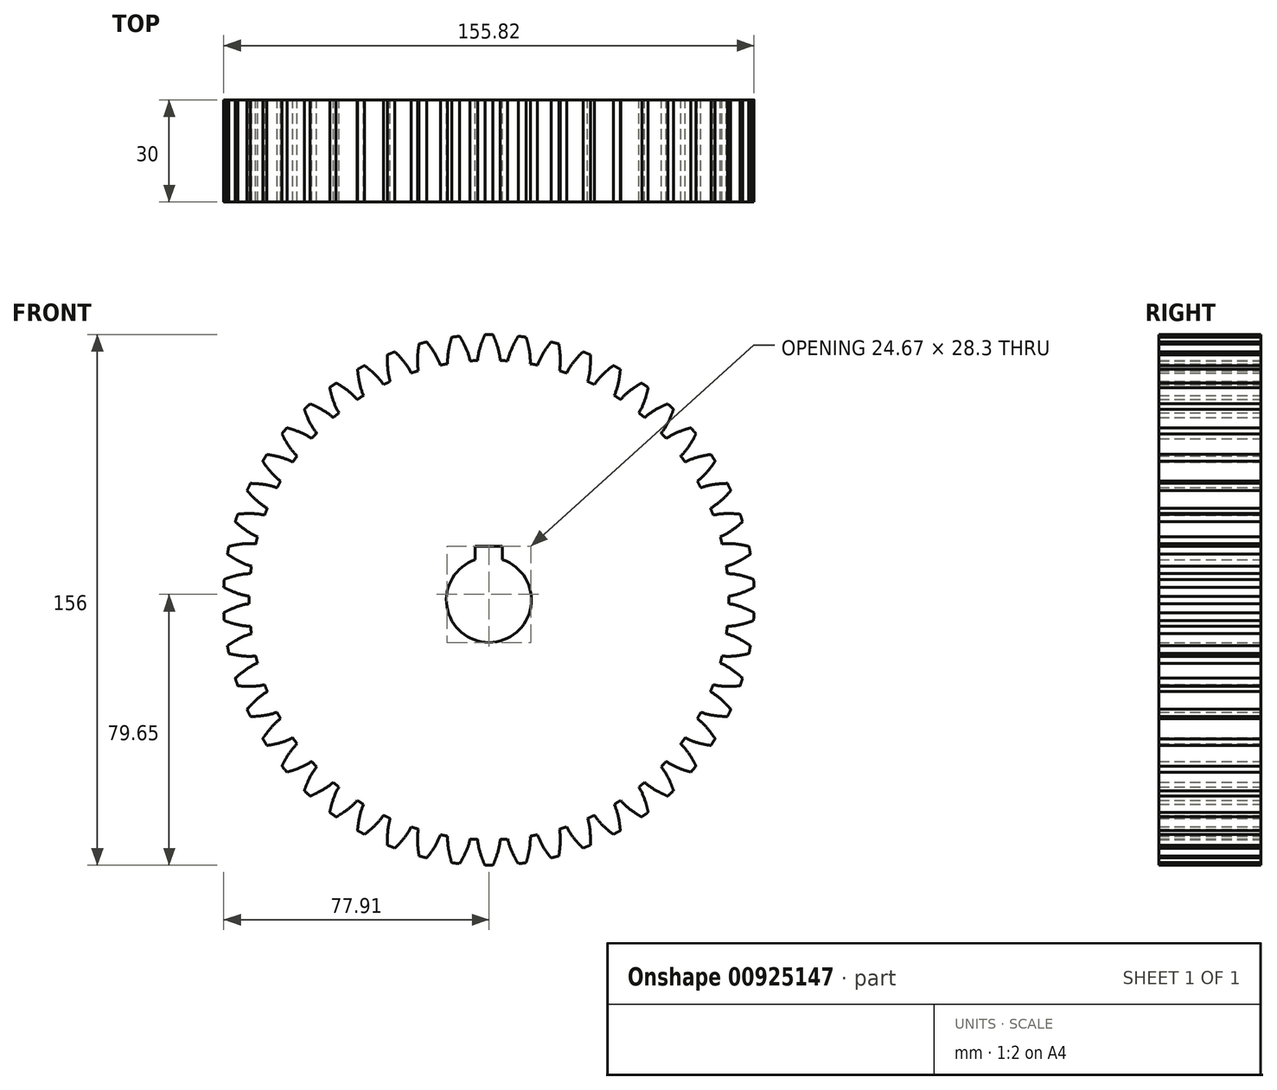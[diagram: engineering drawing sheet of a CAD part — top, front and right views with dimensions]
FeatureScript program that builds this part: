
annotation { "Feature Type Name" : "Feature", "Feature Type Description" : "" }
export const myFeature = defineFeature(function(context is Context, id is Id, definition is map)
    precondition{}
    {
        {
            var Q0;
            Q0=qCreatedBy(makeId("Front.planeOp"),FACE);
            var sketch = newSketch(context, id + "F0", { "sketchPlane" : qUnion([Q0])});
            skCircle(sketch, "E0", {"center": v(0, 0) * mm, "radius": 70.48 * mm});
            skSolve(sketch);
        }
        {
            var Q0;
            Q0 = qSketchRegion(id + "F0", true);
            extrude(context, id + "F1", {"entities" : qUnion([Q0]), "depth" : 30 * mm, "offsetDistance" : 25 * mm});
        }
        {
            var Q0;
            Q0=qCreatedBy(makeId("Front.planeOp"),FACE);
            var sketch = newSketch(context, id + "F2", { "sketchPlane" : qUnion([Q0])});
            skCircle(sketch, "E1", {"center": v(0, 0) * mm, "radius": 75 * mm, "construction": true});
            skArc(sketch, "E2", {"start": v(33.3, 62.11) * mm, "mid": v(22.01, 66.95) * mm, "end": v(10.05, 69.76) * mm, "construction": true});
            skLineSegment(sketch, "E3", {"start": v(-2.36, 74.96) * mm, "end": v(2.36, 74.96) * mm, "construction": true});
            skLineSegment(sketch, "E4", {"start": v(0, 0) * mm, "end": v(-2.36, 74.96) * mm, "construction": true});
            skLineSegment(sketch, "E5", {"start": v(-2.36, 74.96) * mm, "end": v(22.01, 66.95) * mm, "construction": true});
            skLineSegment(sketch, "E6", {"start": v(0, 0) * mm, "end": v(22.01, 66.95) * mm, "construction": true});
            skLineSegment(sketch, "E7.1.0", {"start": v(0, 0) * mm, "end": v(24.34, 66.14) * mm, "construction": true});
            skLineSegment(sketch, "E7.1.1", {"start": v(0.26, 75) * mm, "end": v(24.34, 66.14) * mm, "construction": true});
            skLineSegment(sketch, "E7.2.0", {"start": v(0, 0) * mm, "end": v(26.63, 65.25) * mm, "construction": true});
            skLineSegment(sketch, "E7.2.1", {"start": v(2.88, 74.94) * mm, "end": v(26.63, 65.25) * mm, "construction": true});
            skLineSegment(sketch, "E7.3.0", {"start": v(0, 0) * mm, "end": v(28.89, 64.28) * mm, "construction": true});
            skLineSegment(sketch, "E7.3.1", {"start": v(5.5, 74.8) * mm, "end": v(28.89, 64.28) * mm, "construction": true});
            skLineSegment(sketch, "E7.4.0", {"start": v(0, 0) * mm, "end": v(31.12, 63.24) * mm, "construction": true});
            skLineSegment(sketch, "E7.4.1", {"start": v(8.1, 74.56) * mm, "end": v(31.12, 63.24) * mm, "construction": true});
            skLineSegment(sketch, "E7.5.0", {"start": v(0, 0) * mm, "end": v(33.3, 62.11) * mm, "construction": true});
            skLineSegment(sketch, "E7.5.1", {"start": v(10.7, 74.23) * mm, "end": v(33.3, 62.11) * mm, "construction": true});
            skLineSegment(sketch, "E7.anchor2", {"start": v(0, 0) * mm, "end": v(10.7, 74.23) * mm, "construction": true});
            skLineSegment(sketch, "E8.5.1", {"start": v(0, 0) * mm, "end": v(10.05, 69.76) * mm, "construction": true});
            skLineSegment(sketch, "E9", {"start": v(0.26, 75) * mm, "end": v(-2.05, 75.85) * mm, "construction": true});
            skLineSegment(sketch, "E10", {"start": v(2.88, 74.94) * mm, "end": v(-1.68, 76.8) * mm, "construction": true});
            skLineSegment(sketch, "E11", {"start": v(5.5, 74.8) * mm, "end": v(-1.24, 77.82) * mm, "construction": true});
            skLineSegment(sketch, "E12", {"start": v(8.1, 74.56) * mm, "end": v(-0.73, 78.9) * mm, "construction": true});
            skLineSegment(sketch, "E13", {"start": v(10.7, 74.23) * mm, "end": v(-0.14, 80.05) * mm, "construction": true});
            skFitSpline(sketch, "E14", {"points": [v(-2.36, 74.96) * mm, v(-2.05, 75.85) * mm, v(-1.68, 76.8) * mm, v(-1.24, 77.82) * mm, v(-0.73, 78.9) * mm, v(-0.14, 80.05) * mm], "startDerivative": vector(5.03, 14.43) * mm, "endDerivative": vector(8.17, 15.89) * mm});
            skArc(sketch, "E15", {"start": v(-2.36, 74.96) * mm, "mid": v(-2.99, 72.71) * mm, "end": v(-3.33, 70.4) * mm});
            skFitSpline(sketch, "E16.MirrorCS", {"points": [v(2.36, 74.96) * mm, v(2.05, 75.85) * mm, v(1.68, 76.8) * mm, v(1.24, 77.82) * mm, v(0.73, 78.9) * mm, v(0.14, 80.05) * mm], "startDerivative": vector(-5.03, 14.43) * mm, "endDerivative": vector(-8.17, 15.89) * mm});
            skArc(sketch, "E17.MirrorCS", {"start": v(2.36, 74.96) * mm, "mid": v(2.99, 72.71) * mm, "end": v(3.33, 70.4) * mm});
            skArc(sketch, "E18", {"start": v(1.16, 78) * mm, "mid": v(0, 78) * mm, "end": v(-1.16, 78) * mm});
            skArc(sketch, "E19.trimOffspring", {"start": v(3.33, 70.4) * mm, "mid": v(0, 70.48) * mm, "end": v(-3.33, 70.4) * mm});
            skSolve(sketch);
        }
        {
            var Q0;
            Q0 = qSketchRegion(id + "F2", true);
            var Q1;
            Q1 = qConstructionFilter(qBodyType(qCreatedBy(id + "F2" ,EDGE), BodyType.WIRE), ConstructionObject.NO);
            var Q2;
            Q2=makeQuery(id+"F1.opExtrude","CAP_FACE",FACE,{"disambiguationData":[OSD([sQuery(id+"F0.wireOp",EDGE,"E0")])],"isStart":false});
            extrude(context, id + "F3", {"entities" : qUnion([Q0]), "surfaceEntities" : qUnion([Q1]), "endBound" : BoundingType.UP_TO_SURFACE, "depth" : 25 * mm, "endBoundEntityFace" : qUnion([Q2]), "offsetDistance" : 25 * mm});
        }
        {
            var Q0;
            Q0=makeQuery(id+"F3.opExtrude","SWEPT_BODY",BODY,{"disambiguationData":[OSD([sQuery(id+"F2.wireOp",EDGE,"E14"),sQuery(id+"F2.wireOp",EDGE,"E15"),sQuery(id+"F2.wireOp",EDGE,"E16.MirrorCS"),sQuery(id+"F2.wireOp",EDGE,"E17.MirrorCS"),sQuery(id+"F2.wireOp",EDGE,"E18"),sQuery(id+"F2.wireOp",EDGE,"E19.trimOffspring")])]});
            var Q1;
            Q1=makeQuery(id+"F1.opExtrude","SWEPT_FACE",FACE,{"disambiguationData":[OSD([sQuery(id+"F0.wireOp",EDGE,"E0")])]});
            var Q2;
            Q2=makeQuery(id+"F1.opExtrude","SWEPT_BODY",BODY,{"disambiguationData":[OSD([sQuery(id+"F0.wireOp",EDGE,"E0")])]});
            circularPattern(context, id + "F4", {"operationType" : NewBodyOperationType.ADD, "entities" : qUnion([Q0]), "axis" : qUnion([Q1]), "angle" : 360 * degree, "instanceCount" : 50, "equalSpace" : true});
        }
        {
            var Q0;
            Q0=qCreatedBy(makeId("Front.planeOp"),FACE);
            var sketch = newSketch(context, id + "F5", { "sketchPlane" : qUnion([Q0])});
            skLineSegment(sketch, "E20.top", {"start": v(-4, 15.8) * mm, "end": v(4, 15.8) * mm});
            skLineSegment(sketch, "E20.left", {"start": v(-4, 11.84) * mm, "end": v(-4, 15.8) * mm});
            skLineSegment(sketch, "E20.right", {"start": v(4, 11.84) * mm, "end": v(4, 11.84) * mm});
            skPoint(sketch, "E21.orphan", {"position": v(-4, 0) * mm});
            skLineSegment(sketch, "E22", {"start": v(4, 11.84) * mm, "end": v(4, 15.8) * mm});
            skArc(sketch, "E23", {"start": v(-4, 11.84) * mm, "mid": v(0, -12.5) * mm, "end": v(4, 11.84) * mm});
            skArc(sketch, "E24", {"start": v(4, 11.84) * mm, "mid": v(0, 12.5) * mm, "end": v(-4, 11.84) * mm, "construction": true});
            skSolve(sketch);
        }
        {
            var Q0;
            Q0 = qSketchRegion(id + "F5", true);
            extrude(context, id + "F6", {"entities" : qUnion([Q0]), "operationType" : NewBodyOperationType.REMOVE, "endBound" : BoundingType.THROUGH_ALL, "depth" : 25 * mm, "offsetDistance" : 25 * mm});
        }
    });
